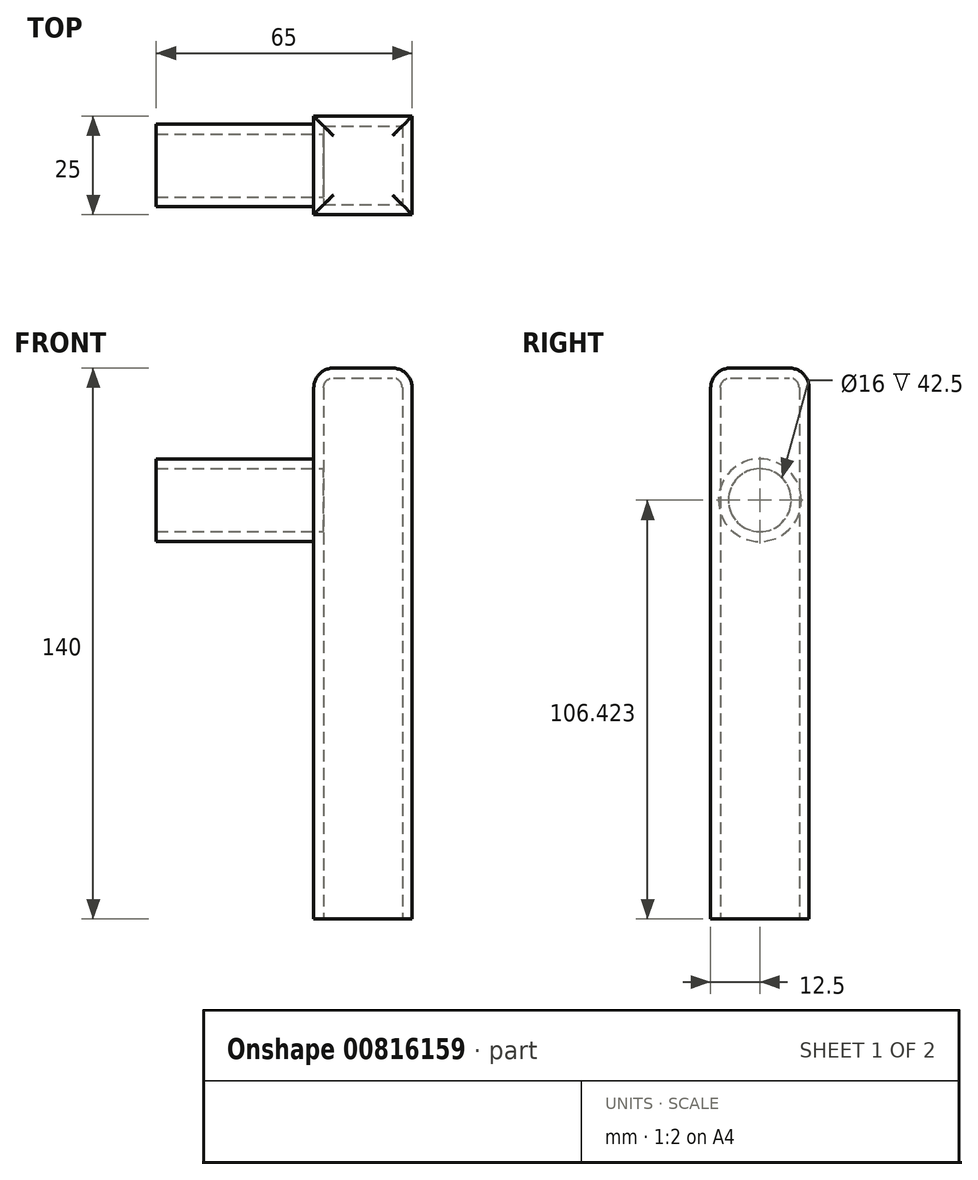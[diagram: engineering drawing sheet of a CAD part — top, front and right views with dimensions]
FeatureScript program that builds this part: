
annotation { "Feature Type Name" : "Feature", "Feature Type Description" : "" }
export const myFeature = defineFeature(function(context is Context, id is Id, definition is map)
    precondition{}
    {
        {
            var Q0;
            Q0=qCreatedBy(makeId("Top.planeOp"),FACE);
            var sketch = newSketch(context, id + "F0", { "sketchPlane" : qUnion([Q0])});
            skLineSegment(sketch, "E0.bottom", {"start": v(-12.5, 12.5) * mm, "end": v(12.5, 12.5) * mm});
            skLineSegment(sketch, "E0.top", {"start": v(-12.5, -12.5) * mm, "end": v(12.5, -12.5) * mm});
            skLineSegment(sketch, "E0.left", {"start": v(-12.5, 12.5) * mm, "end": v(-12.5, -12.5) * mm});
            skLineSegment(sketch, "E0.right", {"start": v(12.5, 12.5) * mm, "end": v(12.5, -12.5) * mm});
            skPoint(sketch, "E0.middle", {"position": v(0, 0) * mm});
            skSolve(sketch);
        }
        {
            var Q0;
            Q0 = qSketchRegion(id + "F0", true);
            extrude(context, id + "F1", {"entities" : qUnion([Q0]), "depth" : 140 * mm, "offsetDistance" : 25 * mm});
        }
        {
            var Q0;
            Q0=makeQuery(id+"F1.opExtrude","CAP_FACE",FACE,{"disambiguationData":[OSD([sQuery(id+"F0.wireOp",EDGE,"E0.bottom"),sQuery(id+"F0.wireOp",EDGE,"E0.top"),sQuery(id+"F0.wireOp",EDGE,"E0.left"),sQuery(id+"F0.wireOp",EDGE,"E0.right")])],"isStart":false});
            fillet(context, id + "F2", {"entities" : qUnion([Q0]), "radius" : 5 * mm, "tangentPropagation" : true, "allowEdgeOverflow" : false});
        }
        {
            var Q0;
            Q0=makeQuery(id+"F1.opExtrude","SWEPT_FACE",FACE,{"disambiguationData":[OSD([sQuery(id+"F0.wireOp",EDGE,"E0.left")])]});
            var sketch = newSketch(context, id + "F3", { "sketchPlane" : qUnion([Q0])});
            skCircle(sketch, "E1", {"center": v(0, 106.42) * mm, "radius": 10.5 * mm});
            skSolve(sketch);
        }
        {
            var Q0;
            Q0=makeQuery(id+"F3.imprint","IMPRINT",FACE,{"disambiguationData":[TD([[makeQuery(id+"F3.imprint","IMPRINT",EDGE,{"derivedFrom":sQuery(id+"F3.wireOp",EDGE,"GlJR6M5D-b3Hu-GW2J-haJt-RaqZ3BlhgdaF")}),1.0]])]});
            var Q1;
            Q1=makeQuery(id+"F3.imprint","IMPRINT",FACE,{"disambiguationData":[TD([[makeQuery(id+"F3.imprint","IMPRINT",EDGE,{"derivedFrom":sQuery(id+"F3.wireOp",EDGE,"E1")}),1.0]])]});
            extrude(context, id + "F4", {"entities" : qUnion([Q0, Q1]), "operationType" : NewBodyOperationType.ADD, "depth" : 40 * mm, "offsetDistance" : 25 * mm});
        }
        {
            var Q0;
            Q0=makeQuery(id+"F1.opExtrude","CAP_FACE",FACE,{"disambiguationData":[OSD([sQuery(id+"F0.wireOp",EDGE,"E0.bottom"),sQuery(id+"F0.wireOp",EDGE,"E0.top"),sQuery(id+"F0.wireOp",EDGE,"E0.left"),sQuery(id+"F0.wireOp",EDGE,"E0.right")])],"isStart":true});
            var Q1;
            Q1=makeQuery(id+"F4.opExtrude","CAP_FACE",FACE,{"disambiguationData":[OSD([sQuery(id+"F3.wireOp",EDGE,"E1")])],"isStart":false});
            shell(context, id + "F5", {"entities" : qUnion([Q0, Q1]), "thickness" : 2.5 * mm});
        }
    });
